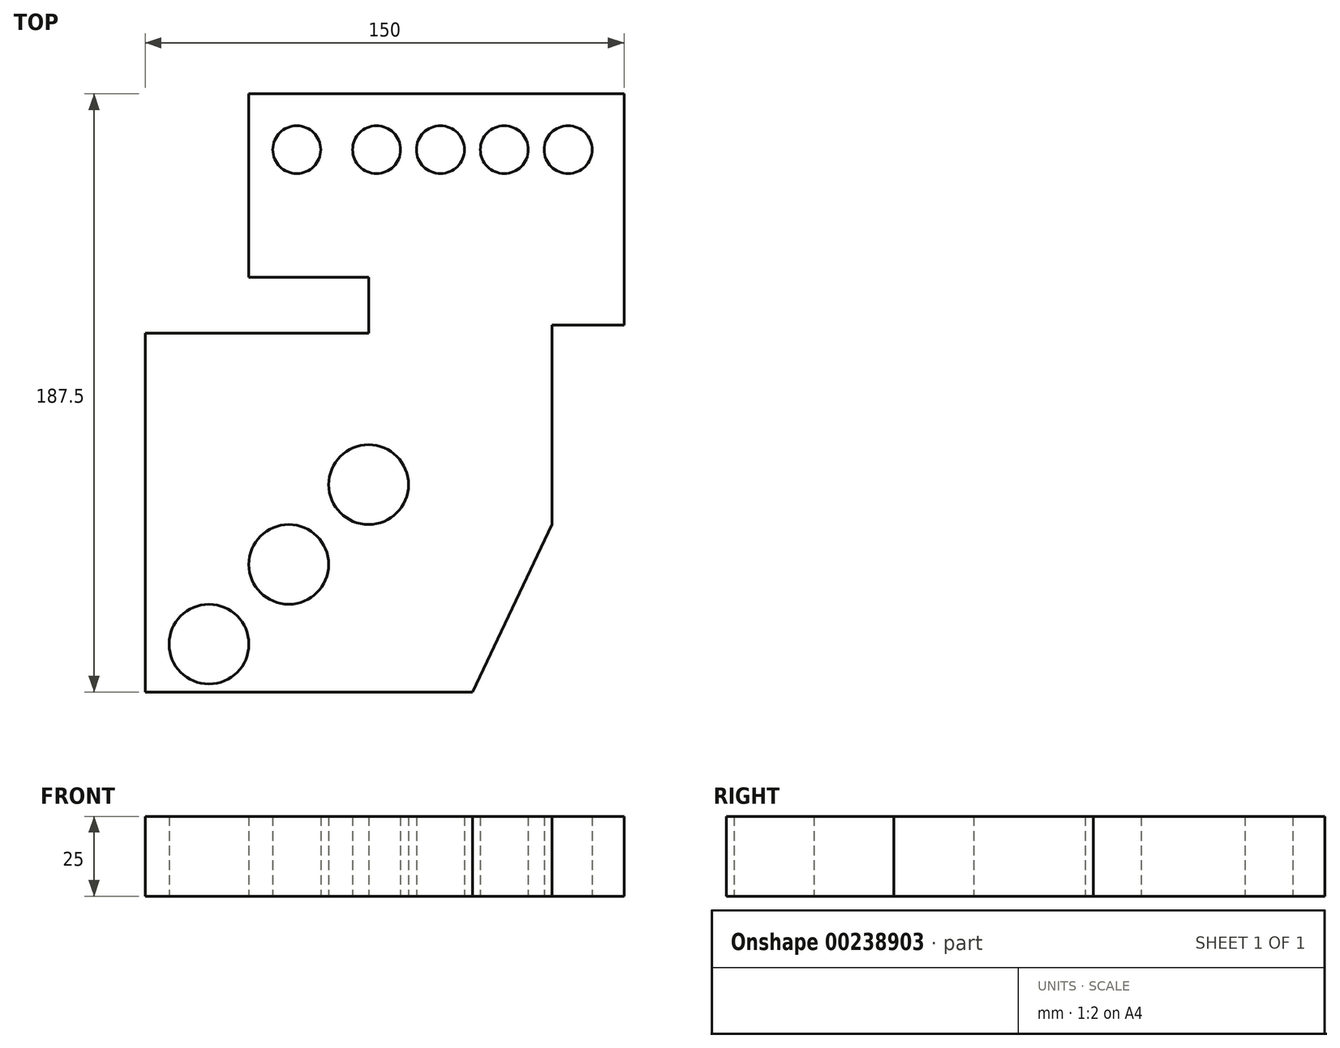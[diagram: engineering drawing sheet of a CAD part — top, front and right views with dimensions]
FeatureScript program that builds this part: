
annotation { "Feature Type Name" : "Feature", "Feature Type Description" : "" }
export const myFeature = defineFeature(function(context is Context, id is Id, definition is map)
    precondition{}
    {
        {
            var Q0;
            Q0=qCreatedBy(makeId("Top.planeOp"),FACE);
            var sketch = newSketch(context, id + "F0", { "sketchPlane" : qUnion([Q0])});
            skLineSegment(sketch, "E0", {"start": v(-38.65, -52.04) * mm, "end": v(63.85, -52.04) * mm});
            skLineSegment(sketch, "E1", {"start": v(-38.65, -52.04) * mm, "end": v(-38.65, 60.46) * mm});
            skLineSegment(sketch, "E2", {"start": v(-38.65, 60.46) * mm, "end": v(31.35, 60.46) * mm});
            skLineSegment(sketch, "E3", {"start": v(31.35, 60.46) * mm, "end": v(31.35, 77.96) * mm});
            skLineSegment(sketch, "E4", {"start": v(31.35, 77.96) * mm, "end": v(-6.15, 77.96) * mm});
            skLineSegment(sketch, "E5", {"start": v(-6.15, 77.96) * mm, "end": v(-6.15, 135.46) * mm});
            skLineSegment(sketch, "E6", {"start": v(-6.15, 135.46) * mm, "end": v(111.35, 135.46) * mm});
            skLineSegment(sketch, "E7", {"start": v(111.35, 135.46) * mm, "end": v(111.35, 62.96) * mm});
            skLineSegment(sketch, "E8", {"start": v(111.35, 62.96) * mm, "end": v(88.85, 62.96) * mm});
            skLineSegment(sketch, "E9", {"start": v(88.85, 62.96) * mm, "end": v(88.85, 0.46) * mm});
            skLineSegment(sketch, "E10", {"start": v(88.85, 0.46) * mm, "end": v(63.85, -52.04) * mm});
            skLineSegment(sketch, "E11", {"start": v(-38.65, -52.04) * mm, "end": v(-38.65, -37.04) * mm});
            skLineSegment(sketch, "E12", {"start": v(-38.65, -37.04) * mm, "end": v(-18.65, -37.04) * mm, "construction": true});
            skLineSegment(sketch, "E13", {"start": v(-18.65, -37.04) * mm, "end": v(-18.65, -52.04) * mm, "construction": true});
            skLineSegment(sketch, "E14", {"start": v(-38.65, -52.04) * mm, "end": v(-38.65, -12.04) * mm, "construction": true});
            skLineSegment(sketch, "E15", {"start": v(-38.65, -12.04) * mm, "end": v(-38.65, 12.96) * mm});
            skLineSegment(sketch, "E16", {"start": v(-18.65, -52.04) * mm, "end": v(6.35, -52.04) * mm});
            skLineSegment(sketch, "E17", {"start": v(6.35, -52.04) * mm, "end": v(31.35, -52.04) * mm});
            skLineSegment(sketch, "E18", {"start": v(6.35, -52.04) * mm, "end": v(6.35, -12.04) * mm, "construction": true});
            skLineSegment(sketch, "E19", {"start": v(6.35, -12.04) * mm, "end": v(-38.65, -12.04) * mm, "construction": true});
            skLineSegment(sketch, "E20", {"start": v(31.35, -52.04) * mm, "end": v(31.35, 12.96) * mm, "construction": true});
            skLineSegment(sketch, "E21", {"start": v(31.35, 12.96) * mm, "end": v(-38.65, 12.96) * mm, "construction": true});
            skCircle(sketch, "E22", {"center": v(-18.65, -37.04) * mm, "radius": 12.5 * mm});
            skCircle(sketch, "E23", {"center": v(6.35, -12.04) * mm, "radius": 12.5 * mm});
            skCircle(sketch, "E24", {"center": v(31.35, 12.96) * mm, "radius": 12.5 * mm});
            skLineSegment(sketch, "E25", {"start": v(111.35, 135.46) * mm, "end": v(111.35, 117.96) * mm});
            skLineSegment(sketch, "E26", {"start": v(111.35, 117.96) * mm, "end": v(93.85, 117.96) * mm, "construction": true});
            skLineSegment(sketch, "E27", {"start": v(93.85, 117.96) * mm, "end": v(73.85, 117.96) * mm, "construction": true});
            skLineSegment(sketch, "E28", {"start": v(73.85, 117.96) * mm, "end": v(53.85, 117.96) * mm, "construction": true});
            skLineSegment(sketch, "E29", {"start": v(53.85, 117.96) * mm, "end": v(33.85, 117.96) * mm, "construction": true});
            skLineSegment(sketch, "E30", {"start": v(33.85, 117.96) * mm, "end": v(8.85, 117.96) * mm, "construction": true});
            skCircle(sketch, "E31", {"center": v(8.85, 117.96) * mm, "radius": 7.5 * mm});
            skCircle(sketch, "E32", {"center": v(33.85, 117.96) * mm, "radius": 7.5 * mm});
            skCircle(sketch, "E33", {"center": v(53.85, 117.96) * mm, "radius": 7.5 * mm});
            skCircle(sketch, "E34", {"center": v(73.85, 117.96) * mm, "radius": 7.5 * mm});
            skCircle(sketch, "E35", {"center": v(93.85, 117.96) * mm, "radius": 7.5 * mm});
            skSolve(sketch);
        }
        {
            var Q0;
            {var subQ3=sQuery(id+"F0.wireOp",EDGE,"E2");Q0=makeQuery(id+"F0.imprint","IMPRINT",FACE,{"disambiguationData":[TD([[makeQuery(id+"F0.imprint","IMPRINT",EDGE,{"derivedFrom":subQ3}),-1.0]])]});}
            extrude(context, id + "F1", {"entities" : qUnion([Q0]), "depth" : 25 * mm});
        }
    });
